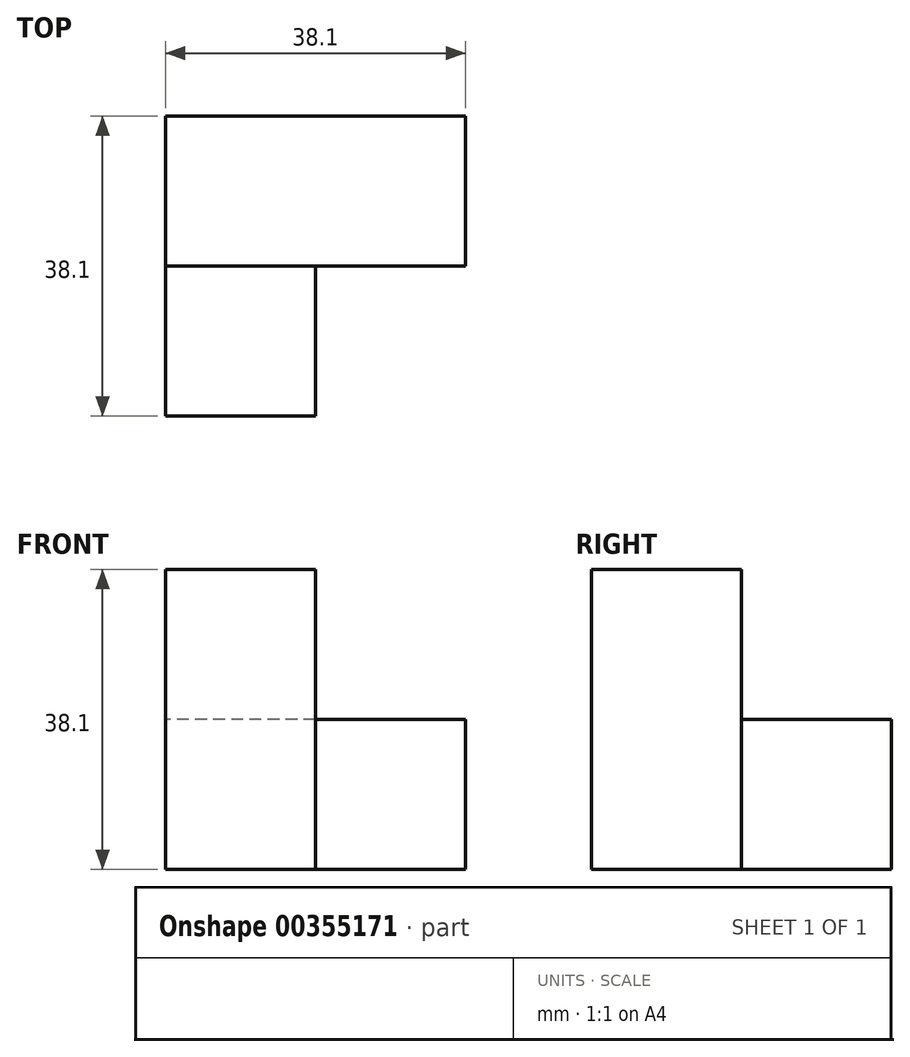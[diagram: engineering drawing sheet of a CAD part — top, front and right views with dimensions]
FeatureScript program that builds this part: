
annotation { "Feature Type Name" : "Feature", "Feature Type Description" : "" }
export const myFeature = defineFeature(function(context is Context, id is Id, definition is map)
    precondition{}
    {
        {
            var Q0;
            Q0=qCreatedBy(makeId("Top.planeOp"),FACE);
            var sketch = newSketch(context, id + "F0", { "sketchPlane" : qUnion([Q0])});
            skLineSegment(sketch, "E0.bottom", {"start": v(0, 0) * mm, "end": v(38.1, 0) * mm});
            skLineSegment(sketch, "E0.top", {"start": v(0, 19.05) * mm, "end": v(38.1, 19.05) * mm});
            skLineSegment(sketch, "E0.left", {"start": v(0, 0) * mm, "end": v(0, 19.05) * mm});
            skLineSegment(sketch, "E0.right", {"start": v(38.1, 0) * mm, "end": v(38.1, 19.05) * mm});
            skPoint(sketch, "E1.oppositeSnap0", {"position": v(19.05, 19.05) * mm});
            skLineSegment(sketch, "E1.bottom", {"start": v(0, 0) * mm, "end": v(19.05, 0) * mm});
            skLineSegment(sketch, "E1.top", {"start": v(0, -19.05) * mm, "end": v(19.05, -19.05) * mm});
            skLineSegment(sketch, "E1.left", {"start": v(0, 0) * mm, "end": v(0, -19.05) * mm});
            skLineSegment(sketch, "E1.right", {"start": v(19.05, 0) * mm, "end": v(19.05, -19.05) * mm});
            skSolve(sketch);
        }
        {
            var Q0;
            Q0 = qSketchRegion(id + "F0", true);
            extrude(context, id + "F1", {"entities" : qUnion([Q0]), "depth" : 19.05 * mm});
        }
        {
            var Q0;
            Q0=qCreatedBy(makeId("Top.planeOp"),FACE);
            var sketch = newSketch(context, id + "F2", { "sketchPlane" : qUnion([Q0])});
            skLineSegment(sketch, "E2.bottom", {"start": v(0, 0) * mm, "end": v(19.05, 0) * mm});
            skLineSegment(sketch, "E2.top", {"start": v(0, -19.05) * mm, "end": v(19.05, -19.05) * mm});
            skLineSegment(sketch, "E2.left", {"start": v(0, 0) * mm, "end": v(0, -19.05) * mm});
            skLineSegment(sketch, "E2.right", {"start": v(19.05, 0) * mm, "end": v(19.05, -19.05) * mm});
            skSolve(sketch);
        }
        {
            var Q0;
            Q0 = qSketchRegion(id + "F2", true);
            extrude(context, id + "F3", {"entities" : qUnion([Q0]), "operationType" : NewBodyOperationType.ADD, "depth" : 38.1 * mm});
        }
    });
